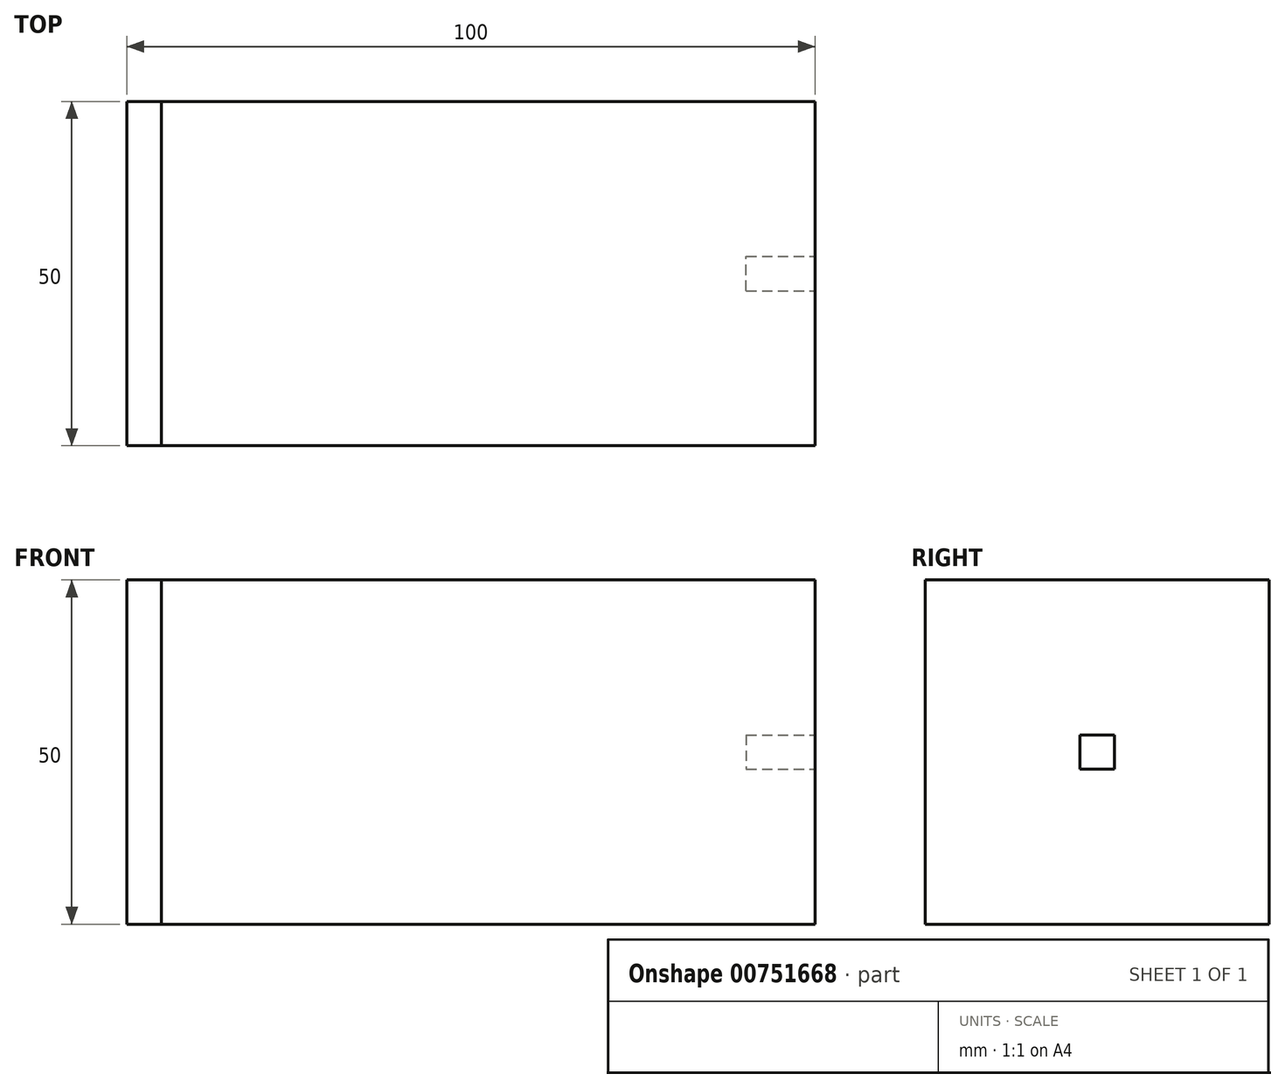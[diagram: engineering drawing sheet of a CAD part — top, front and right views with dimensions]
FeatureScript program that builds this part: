
annotation { "Feature Type Name" : "Feature", "Feature Type Description" : "" }
export const myFeature = defineFeature(function(context is Context, id is Id, definition is map)
    precondition{}
    {
        {
            var Q0;
            Q0=qCreatedBy(makeId("Front.planeOp"),FACE);
            var sketch = newSketch(context, id + "F0", { "sketchPlane" : qUnion([Q0])});
            skLineSegment(sketch, "E0.bottom", {"start": v(0, 0) * mm, "end": v(100, 0) * mm});
            skLineSegment(sketch, "E0.top", {"start": v(0, 50) * mm, "end": v(100, 50) * mm});
            skLineSegment(sketch, "E0.left", {"start": v(0, 0) * mm, "end": v(0, 50) * mm});
            skLineSegment(sketch, "E0.right", {"start": v(100, 0) * mm, "end": v(100, 50) * mm});
            skSolve(sketch);
        }
        {
            var Q0;
            Q0=qSketchRegion(id+"F0",true);
            extrude(context, id + "F1", {"entities" : qUnion([Q0]), "depth" : 50 * mm, "offsetDistance" : 25 * mm});
        }
        {
            var Q0;
            Q0=qCreatedBy(makeId("Right.planeOp"),FACE);
            var sketch = newSketch(context, id + "F2", { "sketchPlane" : qUnion([Q0])});
            skSolve(sketch);
        }
        {
            var Q0;
            Q0=makeQuery(id+"F1.opExtrude","SWEPT_FACE",FACE,{"disambiguationData":[OSD([sQuery(id+"F0.wireOp",EDGE,"E0.left")])]});
            var Q1;
            Q1=qSketchRegion(id+"F2",true);
            extrude(context, id + "F3", {"entities" : qUnion([Q0, Q1]), "oppositeDirection" : true, "depth" : 5 * mm, "offsetDistance" : 25 * mm});
        }
        {
            var Q0;
            Q0=makeQuery(id+"F1.opExtrude","SWEPT_FACE",FACE,{"disambiguationData":[OSD([sQuery(id+"F0.wireOp",EDGE,"E0.right")])]});
            var sketch = newSketch(context, id + "F4", { "sketchPlane" : qUnion([Q0])});
            skLineSegment(sketch, "E1.bottom", {"start": v(-27.5, 27.5) * mm, "end": v(-22.5, 27.5) * mm});
            skLineSegment(sketch, "E1.top", {"start": v(-27.5, 22.5) * mm, "end": v(-22.5, 22.5) * mm});
            skLineSegment(sketch, "E1.left", {"start": v(-27.5, 27.5) * mm, "end": v(-27.5, 22.5) * mm});
            skLineSegment(sketch, "E1.right", {"start": v(-22.5, 27.5) * mm, "end": v(-22.5, 22.5) * mm});
            skLineSegment(sketch, "E2", {"start": v(-25, 50) * mm, "end": v(-25, 0) * mm, "construction": true});
            skLineSegment(sketch, "E3", {"start": v(-50, 25) * mm, "end": v(0, 25) * mm, "construction": true});
            skSolve(sketch);
        }
        {
            var Q0;
            Q0=qSketchRegion(id+"F4",true);
            extrude(context, id + "F5", {"entities" : qUnion([Q0]), "oppositeDirection" : true, "depth" : 10 * mm, "offsetDistance" : 25 * mm});
        }
    });
